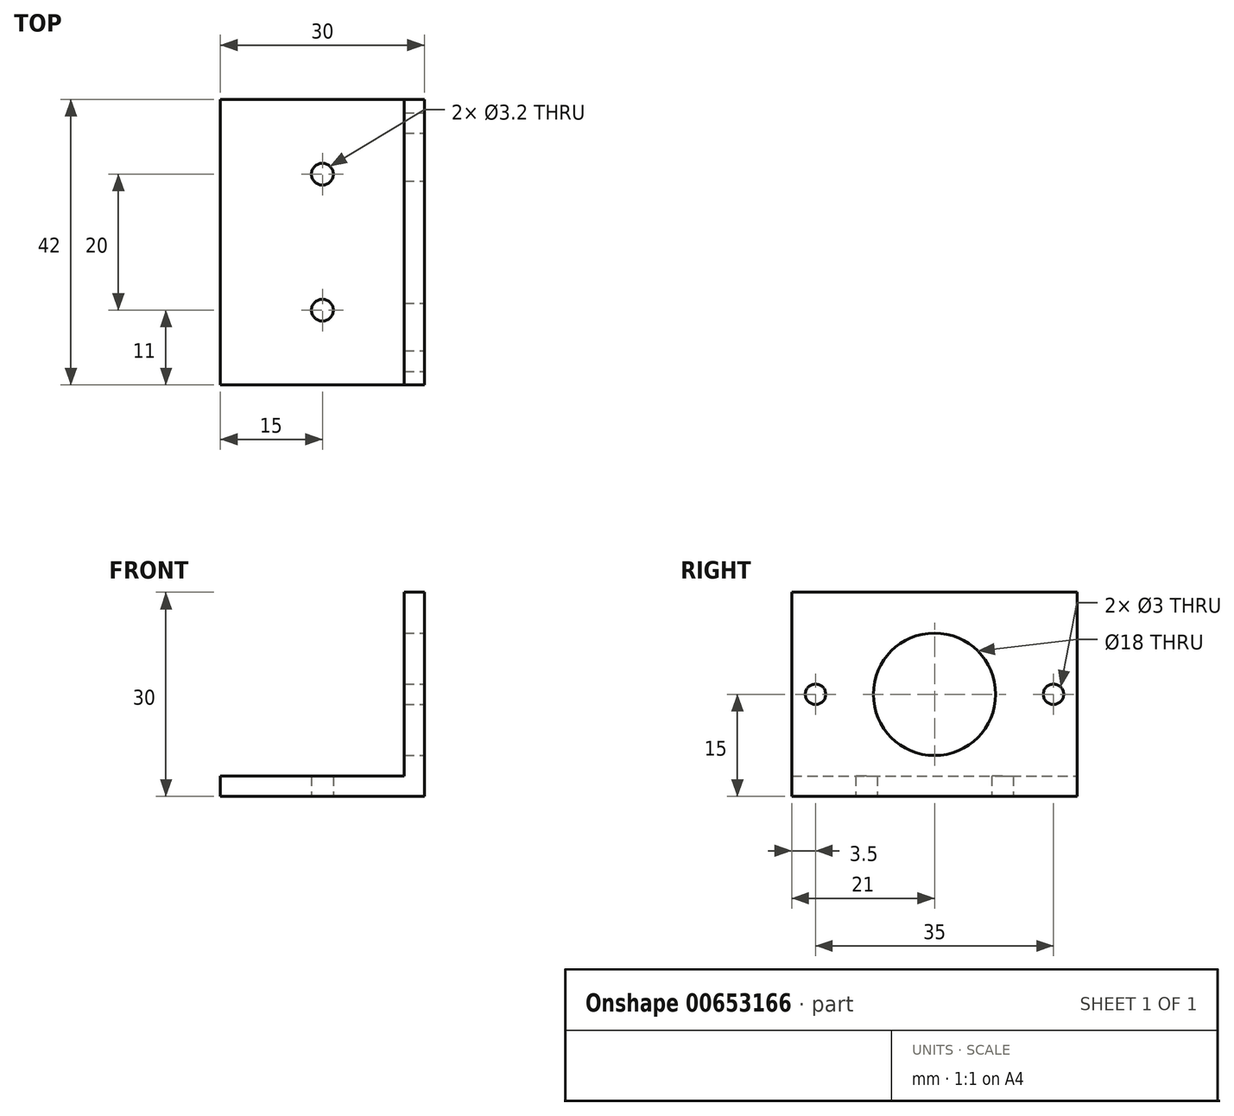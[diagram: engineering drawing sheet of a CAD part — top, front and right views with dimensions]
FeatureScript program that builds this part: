
annotation { "Feature Type Name" : "Feature", "Feature Type Description" : "" }
export const myFeature = defineFeature(function(context is Context, id is Id, definition is map)
    precondition{}
    {
        {
            var Q0;
            Q0=qCreatedBy(makeId("Front.planeOp"),FACE);
            var sketch = newSketch(context, id + "F0", { "sketchPlane" : qUnion([Q0])});
            skLineSegment(sketch, "E0", {"start": v(0, 30) * mm, "end": v(0, 0) * mm});
            skLineSegment(sketch, "E1", {"start": v(0, 0) * mm, "end": v(-30, 0) * mm});
            skLineSegment(sketch, "E2", {"start": v(-30, 0) * mm, "end": v(-30, 3) * mm});
            skLineSegment(sketch, "E3", {"start": v(-30, 3) * mm, "end": v(-3, 3) * mm});
            skLineSegment(sketch, "E4", {"start": v(-3, 3) * mm, "end": v(-3, 30) * mm});
            skLineSegment(sketch, "E5", {"start": v(-3, 30) * mm, "end": v(0, 30) * mm});
            skSolve(sketch);
        }
        {
            var Q0;
            Q0 = qSketchRegion(id + "F0", true);
            extrude(context, id + "F1", {"entities" : qUnion([Q0]), "depth" : 42 * mm, "offsetDistance" : 25 * mm});
        }
        {
            var Q0;
            Q0=makeQuery(id+"F1.opExtrude","SWEPT_FACE",FACE,{"disambiguationData":[OSD([sQuery(id+"F0.wireOp",EDGE,"E0")])]});
            var sketch = newSketch(context, id + "F2", { "sketchPlane" : qUnion([Q0])});
            skLineSegment(sketch, "E6", {"start": v(-21, 66.4) * mm, "end": v(-21, -29.44) * mm, "construction": true});
            skLineSegment(sketch, "E7", {"start": v(-83.8, 15) * mm, "end": v(40.42, 15) * mm, "construction": true});
            skCircle(sketch, "E8", {"center": v(-21, 15) * mm, "radius": 9 * mm});
            skCircle(sketch, "E9", {"center": v(-3.5, 15) * mm, "radius": 1.5 * mm});
            skCircle(sketch, "E10", {"center": v(-38.5, 15) * mm, "radius": 1.5 * mm});
            skSolve(sketch);
        }
        {
            var Q0;
            Q0 = qSketchRegion(id + "F2", true);
            extrude(context, id + "F3", {"entities" : qUnion([Q0]), "operationType" : NewBodyOperationType.REMOVE, "endBound" : BoundingType.THROUGH_ALL, "oppositeDirection" : true, "depth" : 25 * mm, "offsetDistance" : 25 * mm});
        }
        {
            var Q0;
            Q0=makeQuery(id+"F1.opExtrude","SWEPT_FACE",FACE,{"disambiguationData":[OSD([sQuery(id+"F0.wireOp",EDGE,"E1")])]});
            var sketch = newSketch(context, id + "F4", { "sketchPlane" : qUnion([Q0])});
            skLineSegment(sketch, "E11", {"start": v(-15, 2.18) * mm, "end": v(-15, 38.82) * mm, "construction": true});
            skLineSegment(sketch, "E12", {"start": v(2.06, 21) * mm, "end": v(-33.33, 21) * mm, "construction": true});
            skCircle(sketch, "E13", {"center": v(-15, 11) * mm, "radius": 1.6 * mm});
            skCircle(sketch, "E14", {"center": v(-15, 31) * mm, "radius": 1.6 * mm});
            skSolve(sketch);
        }
        {
            var Q0;
            Q0 = qSketchRegion(id + "F4", true);
            extrude(context, id + "F5", {"entities" : qUnion([Q0]), "operationType" : NewBodyOperationType.REMOVE, "endBound" : BoundingType.THROUGH_ALL, "oppositeDirection" : true, "depth" : 25 * mm, "offsetDistance" : 25 * mm});
        }
    });
